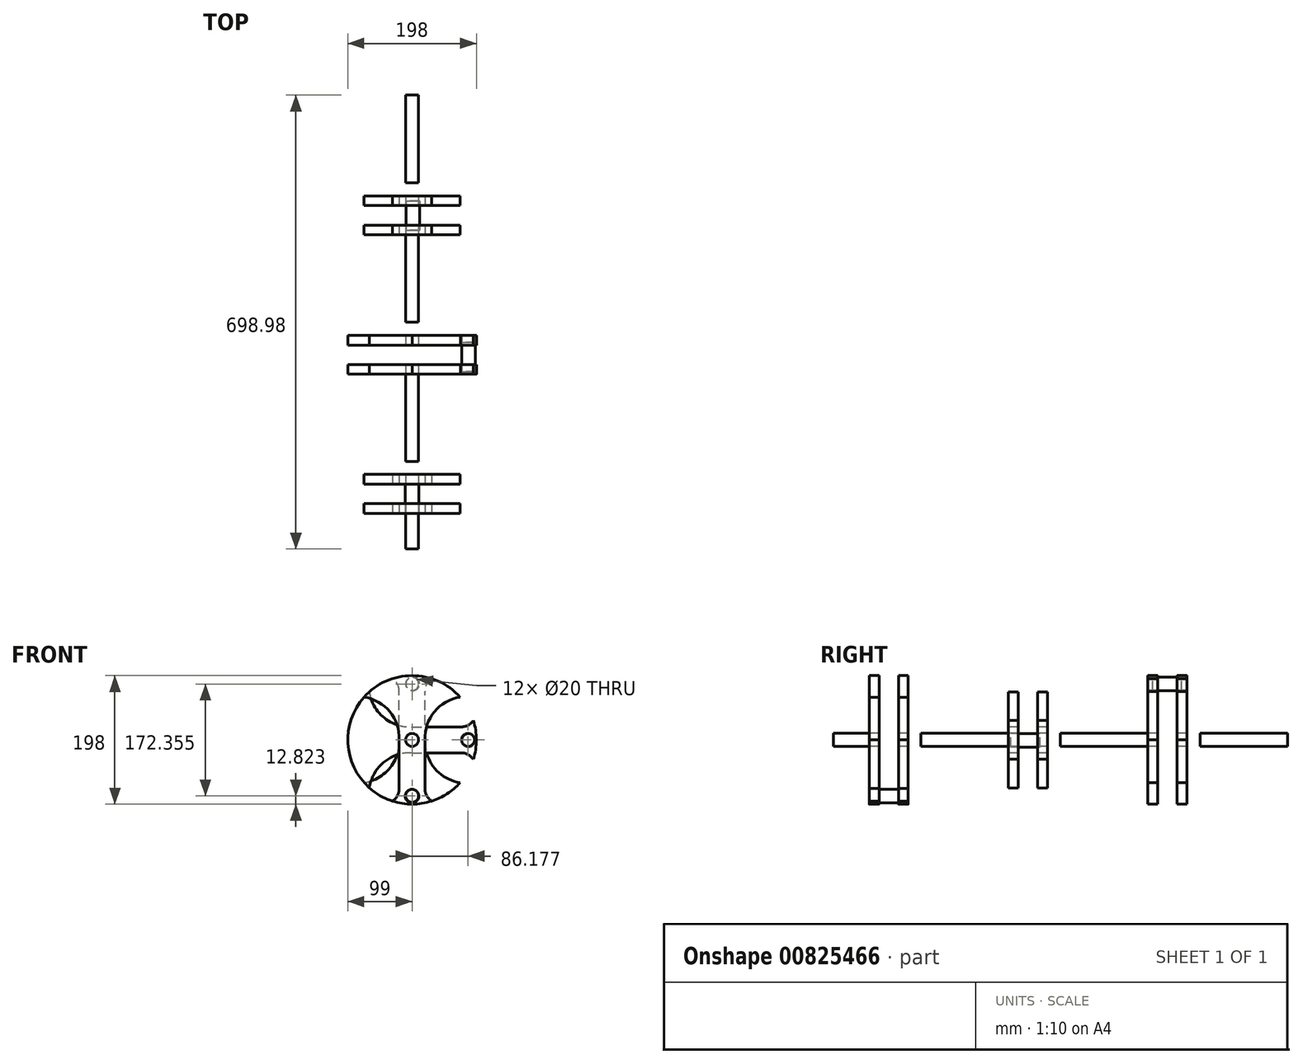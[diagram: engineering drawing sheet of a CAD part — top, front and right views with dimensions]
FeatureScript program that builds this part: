
annotation { "Feature Type Name" : "Feature", "Feature Type Description" : "" }
export const myFeature = defineFeature(function(context is Context, id is Id, definition is map)
    precondition{}
    {
        {
            var Q0;
            Q0=qCreatedBy(makeId("Front.planeOp"),FACE);
            var sketch = newSketch(context, id + "F0", { "sketchPlane" : qUnion([Q0])});
            skCircle(sketch, "E0", {"center": v(0, 0) * mm, "radius": 10 * mm});
            skSolve(sketch);
        }
        {
            var Q0;
            Q0 = qSketchRegion(id + "F0", true);
            extrude(context, id + "F1", {"entities" : qUnion([Q0]), "depth" : 135 * mm, "offsetDistance" : 25 * mm});
        }
        {
            var Q0;
            Q0=makeQuery(id+"F1.opExtrude","CAP_FACE",FACE,{"disambiguationData":[OSD([sQuery(id+"F0.wireOp",EDGE,"E0")])],"isStart":true});
            var sketch = newSketch(context, id + "F2", { "sketchPlane" : qUnion([Q0])});
            skArc(sketch, "E1", {"start": v(-30, -94.35) * mm, "mid": v(0, -99) * mm, "end": v(30, -94.35) * mm});
            skArc(sketch, "E2", {"start": v(-20, 0) * mm, "mid": v(-34.3, 43.3) * mm, "end": v(-73.91, 65.86) * mm});
            skLineSegment(sketch, "E3", {"start": v(-20, 0) * mm, "end": v(-20, -76.74) * mm});
            skArc(sketch, "E4", {"start": v(-30, -94.35) * mm, "mid": v(-22.41, -85.87) * mm, "end": v(-20, -74.76) * mm});
            skArc(sketch, "E5.MirrorCS", {"start": v(20, 0) * mm, "mid": v(34.3, 43.3) * mm, "end": v(73.91, 65.86) * mm});
            skLineSegment(sketch, "E6.MirrorCS", {"start": v(20, 0) * mm, "end": v(20, -76.74) * mm});
            skArc(sketch, "E7.MirrorCS", {"start": v(30, -94.35) * mm, "mid": v(22.41, -85.87) * mm, "end": v(20, -74.76) * mm});
            skArc(sketch, "E8.trimOffspring", {"start": v(73.91, 65.86) * mm, "mid": v(0, 99) * mm, "end": v(-73.91, 65.86) * mm});
            skPoint(sketch, "E9", {"position": v(0, -86.18) * mm});
            skPoint(sketch, "E9.positionSnap0", {"position": v(0, -99) * mm});
            skCircle(sketch, "E10", {"center": v(0, -86.18) * mm, "radius": 10 * mm});
            skSolve(sketch);
        }
        {
            var Q0;
            {var subQ4=sQuery(id+"F2.wireOp",EDGE,"E1");Q0=makeQuery(id+"F2.imprint","IMPRINT",FACE,{"disambiguationData":[TD([[makeQuery(id+"F2.imprint","IMPRINT",EDGE,{"derivedFrom":subQ4}),1.0]])]});}
            extrude(context, id + "F3", {"entities" : qUnion([Q0]), "depth" : 15 * mm, "offsetDistance" : 25 * mm});
        }
        {
            var Q0;
            Q0=makeQuery(id+"F3.opExtrude","SWEPT_BODY",BODY,{"disambiguationData":[OSD([sQuery(id+"F0.wireOp",EDGE,"E0"),sQuery(id+"F2.wireOp",EDGE,"E1"),sQuery(id+"F2.wireOp",EDGE,"E2"),sQuery(id+"F2.wireOp",EDGE,"E3"),sQuery(id+"F2.wireOp",EDGE,"E4"),sQuery(id+"F2.wireOp",EDGE,"E5.MirrorCS"),sQuery(id+"F2.wireOp",EDGE,"E6.MirrorCS"),sQuery(id+"F2.wireOp",EDGE,"E7.MirrorCS"),sQuery(id+"F2.wireOp",EDGE,"E8.trimOffspring"),sQuery(id+"F2.wireOp",EDGE,"E10")])]});
            transform(context, id + "F4", {"entities" : qUnion([Q0]), "transformType" : TransformType.TRANSLATION_3D, "dx" : 0 * mm, "dy" : 0 * mm, "dz" : 0 * mm, "makeCopy" : true});
        }
        {
            var Q0;
            Q0=makeQuery(id+"F3.opExtrude","SWEPT_BODY",BODY,{"disambiguationData":[OSD([sQuery(id+"F0.wireOp",EDGE,"E0"),sQuery(id+"F2.wireOp",EDGE,"E1"),sQuery(id+"F2.wireOp",EDGE,"E2"),sQuery(id+"F2.wireOp",EDGE,"E3"),sQuery(id+"F2.wireOp",EDGE,"E4"),sQuery(id+"F2.wireOp",EDGE,"E5.MirrorCS"),sQuery(id+"F2.wireOp",EDGE,"E6.MirrorCS"),sQuery(id+"F2.wireOp",EDGE,"E7.MirrorCS"),sQuery(id+"F2.wireOp",EDGE,"E8.trimOffspring"),sQuery(id+"F2.wireOp",EDGE,"E10")])]});
            transform(context, id + "F5", {"entities" : qUnion([Q0]), "transformType" : TransformType.TRANSLATION_3D, "dx" : 0 * mm, "dy" : 0 * mm, "dz" : 36 * mm, "makeCopy" : true});
        }
        {
            var Q0;
            Q0=makeQuery(id+"F5.opPattern","COPY",BODY,{"derivedFrom":makeQuery(id+"F3.opExtrude","SWEPT_BODY",BODY,{"disambiguationData":[OSD([sQuery(id+"F0.wireOp",EDGE,"E0"),sQuery(id+"F2.wireOp",EDGE,"E1"),sQuery(id+"F2.wireOp",EDGE,"E2"),sQuery(id+"F2.wireOp",EDGE,"E3"),sQuery(id+"F2.wireOp",EDGE,"E4"),sQuery(id+"F2.wireOp",EDGE,"E5.MirrorCS"),sQuery(id+"F2.wireOp",EDGE,"E6.MirrorCS"),sQuery(id+"F2.wireOp",EDGE,"E7.MirrorCS"),sQuery(id+"F2.wireOp",EDGE,"E8.trimOffspring"),sQuery(id+"F2.wireOp",EDGE,"E10")])]}),"instanceName":"1"});
            deleteBodies(context, id + "F6", {"entities" : qUnion([Q0])});
        }
        {
            var Q0;
            Q0=makeQuery(id+"F4.opPattern","COPY",BODY,{"derivedFrom":makeQuery(id+"F3.opExtrude","SWEPT_BODY",BODY,{"disambiguationData":[OSD([sQuery(id+"F0.wireOp",EDGE,"E0"),sQuery(id+"F2.wireOp",EDGE,"E1"),sQuery(id+"F2.wireOp",EDGE,"E2"),sQuery(id+"F2.wireOp",EDGE,"E3"),sQuery(id+"F2.wireOp",EDGE,"E4"),sQuery(id+"F2.wireOp",EDGE,"E5.MirrorCS"),sQuery(id+"F2.wireOp",EDGE,"E6.MirrorCS"),sQuery(id+"F2.wireOp",EDGE,"E7.MirrorCS"),sQuery(id+"F2.wireOp",EDGE,"E8.trimOffspring"),sQuery(id+"F2.wireOp",EDGE,"E10")])]}),"instanceName":"1"});
            deleteBodies(context, id + "F7", {"entities" : qUnion([Q0])});
        }
        {
            var Q0;
            Q0=makeQuery(id+"F3.opExtrude","SWEPT_BODY",BODY,{"disambiguationData":[OSD([sQuery(id+"F0.wireOp",EDGE,"E0"),sQuery(id+"F2.wireOp",EDGE,"E1"),sQuery(id+"F2.wireOp",EDGE,"E2"),sQuery(id+"F2.wireOp",EDGE,"E3"),sQuery(id+"F2.wireOp",EDGE,"E4"),sQuery(id+"F2.wireOp",EDGE,"E5.MirrorCS"),sQuery(id+"F2.wireOp",EDGE,"E6.MirrorCS"),sQuery(id+"F2.wireOp",EDGE,"E7.MirrorCS"),sQuery(id+"F2.wireOp",EDGE,"E8.trimOffspring"),sQuery(id+"F2.wireOp",EDGE,"E10")])]});
            transform(context, id + "F8", {"entities" : qUnion([Q0]), "transformType" : TransformType.TRANSLATION_3D, "dx" : 36 * mm, "dy" : 0 * mm, "dz" : 0 * mm, "makeCopy" : true});
        }
        {
            var Q0;
            Q0=makeQuery(id+"F8.opPattern","COPY",BODY,{"derivedFrom":makeQuery(id+"F3.opExtrude","SWEPT_BODY",BODY,{"disambiguationData":[OSD([sQuery(id+"F0.wireOp",EDGE,"E0"),sQuery(id+"F2.wireOp",EDGE,"E1"),sQuery(id+"F2.wireOp",EDGE,"E2"),sQuery(id+"F2.wireOp",EDGE,"E3"),sQuery(id+"F2.wireOp",EDGE,"E4"),sQuery(id+"F2.wireOp",EDGE,"E5.MirrorCS"),sQuery(id+"F2.wireOp",EDGE,"E6.MirrorCS"),sQuery(id+"F2.wireOp",EDGE,"E7.MirrorCS"),sQuery(id+"F2.wireOp",EDGE,"E8.trimOffspring"),sQuery(id+"F2.wireOp",EDGE,"E10")])]}),"instanceName":"1"});
            deleteBodies(context, id + "F9", {"entities" : qUnion([Q0])});
        }
        {
            var Q0;
            Q0=makeQuery(id+"F3.opExtrude","SWEPT_BODY",BODY,{"disambiguationData":[OSD([sQuery(id+"F0.wireOp",EDGE,"E0"),sQuery(id+"F2.wireOp",EDGE,"E1"),sQuery(id+"F2.wireOp",EDGE,"E2"),sQuery(id+"F2.wireOp",EDGE,"E3"),sQuery(id+"F2.wireOp",EDGE,"E4"),sQuery(id+"F2.wireOp",EDGE,"E5.MirrorCS"),sQuery(id+"F2.wireOp",EDGE,"E6.MirrorCS"),sQuery(id+"F2.wireOp",EDGE,"E7.MirrorCS"),sQuery(id+"F2.wireOp",EDGE,"E8.trimOffspring"),sQuery(id+"F2.wireOp",EDGE,"E10")])]});
            transform(context, id + "F10", {"entities" : qUnion([Q0]), "transformType" : TransformType.TRANSLATION_3D, "dx" : 0 * mm, "dy" : 36 * mm, "dz" : 0 * mm, "makeCopy" : true});
        }
        {
            var Q0;
            Q0=makeQuery(id+"F10.opPattern","COPY",BODY,{"derivedFrom":makeQuery(id+"F3.opExtrude","SWEPT_BODY",BODY,{"disambiguationData":[OSD([sQuery(id+"F0.wireOp",EDGE,"E0"),sQuery(id+"F2.wireOp",EDGE,"E1"),sQuery(id+"F2.wireOp",EDGE,"E2"),sQuery(id+"F2.wireOp",EDGE,"E3"),sQuery(id+"F2.wireOp",EDGE,"E4"),sQuery(id+"F2.wireOp",EDGE,"E5.MirrorCS"),sQuery(id+"F2.wireOp",EDGE,"E6.MirrorCS"),sQuery(id+"F2.wireOp",EDGE,"E7.MirrorCS"),sQuery(id+"F2.wireOp",EDGE,"E8.trimOffspring"),sQuery(id+"F2.wireOp",EDGE,"E10")])]}),"instanceName":"1"});
            deleteBodies(context, id + "F11", {"entities" : qUnion([Q0])});
        }
        {
            var Q0;
            Q0=qCreatedBy(makeId("Front.planeOp"),FACE);
            var sketch = newSketch(context, id + "F12", { "sketchPlane" : qUnion([Q0])});
            skCircle(sketch, "E11", {"center": v(0, -86.64) * mm, "radius": 10.47 * mm});
            skSolve(sketch);
        }
        {
            var Q0;
            Q0=makeQuery(id+"F12.imprint","IMPRINT",FACE,{"disambiguationData":[TD([[makeQuery(id+"F12.imprint","IMPRINT",EDGE,{"derivedFrom":sQuery(id+"F12.wireOp",EDGE,"E11")}),1.0]])]});
            var Q1;
            Q1=sQuery(id+"F12.wireOp",EDGE,"E11");
            extrude(context, id + "F13", {"entities" : qUnion([Q0]), "surfaceEntities" : qUnion([Q1]), "oppositeDirection" : true, "depth" : 45 * mm, "offsetDistance" : 25 * mm});
        }
        {
            var Q0;
            Q0=makeQuery(id+"F3.opExtrude","SWEPT_BODY",BODY,{"disambiguationData":[OSD([sQuery(id+"F0.wireOp",EDGE,"E0"),sQuery(id+"F2.wireOp",EDGE,"E1"),sQuery(id+"F2.wireOp",EDGE,"E2"),sQuery(id+"F2.wireOp",EDGE,"E3"),sQuery(id+"F2.wireOp",EDGE,"E4"),sQuery(id+"F2.wireOp",EDGE,"E5.MirrorCS"),sQuery(id+"F2.wireOp",EDGE,"E6.MirrorCS"),sQuery(id+"F2.wireOp",EDGE,"E7.MirrorCS"),sQuery(id+"F2.wireOp",EDGE,"E8.trimOffspring"),sQuery(id+"F2.wireOp",EDGE,"E10")])]});
            transform(context, id + "F14", {"entities" : qUnion([Q0]), "transformType" : TransformType.TRANSLATION_3D, "dx" : 0 * mm, "dy" : 30.5 * mm, "dz" : 0 * mm, "makeCopy" : true});
        }
        {
            var Q0;
            Q0=makeQuery(id+"F1.opExtrude","SWEPT_BODY",BODY,{"disambiguationData":[OSD([sQuery(id+"F0.wireOp",EDGE,"E0")])]});
            transform(context, id + "F15", {"entities" : qUnion([Q0]), "transformType" : TransformType.TRANSLATION_3D, "dx" : 0 * mm, "dy" : 131.5 * mm, "dz" : 0 * mm, "makeCopy" : true});
        }
        {
            var Q0;
            Q0=makeQuery(id+"F15.opPattern","COPY",BODY,{"derivedFrom":makeQuery(id+"F1.opExtrude","SWEPT_BODY",BODY,{"disambiguationData":[OSD([sQuery(id+"F0.wireOp",EDGE,"E0")])]}),"instanceName":"1"});
            deleteBodies(context, id + "F16", {"entities" : qUnion([Q0])});
        }
        {
            var Q0;
            Q0=makeQuery(id+"F3.opExtrude","SWEPT_BODY",BODY,{"disambiguationData":[OSD([sQuery(id+"F0.wireOp",EDGE,"E0"),sQuery(id+"F2.wireOp",EDGE,"E1"),sQuery(id+"F2.wireOp",EDGE,"E2"),sQuery(id+"F2.wireOp",EDGE,"E3"),sQuery(id+"F2.wireOp",EDGE,"E4"),sQuery(id+"F2.wireOp",EDGE,"E5.MirrorCS"),sQuery(id+"F2.wireOp",EDGE,"E6.MirrorCS"),sQuery(id+"F2.wireOp",EDGE,"E7.MirrorCS"),sQuery(id+"F2.wireOp",EDGE,"E8.trimOffspring"),sQuery(id+"F2.wireOp",EDGE,"E10")])]});
            transform(context, id + "F17", {"entities" : qUnion([Q0]), "transformType" : TransformType.TRANSLATION_3D, "dx" : 0 * mm, "dy" : 46 * mm, "dz" : 0 * mm, "makeCopy" : true});
        }
        {
            var Q0;
            Q0=makeQuery(id+"F17.opPattern","COPY",BODY,{"derivedFrom":makeQuery(id+"F3.opExtrude","SWEPT_BODY",BODY,{"disambiguationData":[OSD([sQuery(id+"F0.wireOp",EDGE,"E0"),sQuery(id+"F2.wireOp",EDGE,"E1"),sQuery(id+"F2.wireOp",EDGE,"E2"),sQuery(id+"F2.wireOp",EDGE,"E3"),sQuery(id+"F2.wireOp",EDGE,"E4"),sQuery(id+"F2.wireOp",EDGE,"E5.MirrorCS"),sQuery(id+"F2.wireOp",EDGE,"E6.MirrorCS"),sQuery(id+"F2.wireOp",EDGE,"E7.MirrorCS"),sQuery(id+"F2.wireOp",EDGE,"E8.trimOffspring"),sQuery(id+"F2.wireOp",EDGE,"E10")])]}),"instanceName":"1"});
            var Q1;
            Q1=makeQuery(id+"F17.opPattern","COPY",EDGE,{"derivedFrom":makeQuery(id+"F3.opExtrude","CAP_EDGE",EDGE,{"disambiguationData":[OSD([sQuery(id+"F0.wireOp",EDGE,"E0")])],"isStart":false}),"instanceName":"1"});
            transform(context, id + "F18", {"entities" : qUnion([Q0]), "transformType" : TransformType.ROTATION, "transformAxis" : qUnion([Q1]), "angle" : 45 * degree, "makeCopy" : false});
        }
        {
            var Q0;
            Q0=makeQuery(id+"F13.opExtrude","SWEPT_BODY",BODY,{"disambiguationData":[OSD([sQuery(id+"F12.wireOp",EDGE,"E11")])]});
            transform(context, id + "F19", {"entities" : qUnion([Q0]), "transformType" : TransformType.TRANSLATION_3D, "dx" : 61 * mm, "dy" : 46 * mm, "dz" : 26 * mm, "makeCopy" : true});
        }
        {
            var Q0;
            Q0=makeQuery(id+"F17.opPattern","COPY",BODY,{"derivedFrom":makeQuery(id+"F3.opExtrude","SWEPT_BODY",BODY,{"disambiguationData":[OSD([sQuery(id+"F0.wireOp",EDGE,"E0"),sQuery(id+"F2.wireOp",EDGE,"E1"),sQuery(id+"F2.wireOp",EDGE,"E2"),sQuery(id+"F2.wireOp",EDGE,"E3"),sQuery(id+"F2.wireOp",EDGE,"E4"),sQuery(id+"F2.wireOp",EDGE,"E5.MirrorCS"),sQuery(id+"F2.wireOp",EDGE,"E6.MirrorCS"),sQuery(id+"F2.wireOp",EDGE,"E7.MirrorCS"),sQuery(id+"F2.wireOp",EDGE,"E8.trimOffspring"),sQuery(id+"F2.wireOp",EDGE,"E10")])]}),"instanceName":"1"});
            transform(context, id + "F20", {"entities" : qUnion([Q0]), "transformType" : TransformType.TRANSLATION_3D, "dx" : 0 * mm, "dy" : 31.5 * mm, "dz" : 0 * mm, "makeCopy" : true});
        }
        {
            var Q0;
            Q0=makeQuery(id+"F20.opPattern","COPY",BODY,{"derivedFrom":makeQuery(id+"F17.opPattern","COPY",BODY,{"derivedFrom":makeQuery(id+"F3.opExtrude","SWEPT_BODY",BODY,{"disambiguationData":[OSD([sQuery(id+"F0.wireOp",EDGE,"E0"),sQuery(id+"F2.wireOp",EDGE,"E1"),sQuery(id+"F2.wireOp",EDGE,"E2"),sQuery(id+"F2.wireOp",EDGE,"E3"),sQuery(id+"F2.wireOp",EDGE,"E4"),sQuery(id+"F2.wireOp",EDGE,"E5.MirrorCS"),sQuery(id+"F2.wireOp",EDGE,"E6.MirrorCS"),sQuery(id+"F2.wireOp",EDGE,"E7.MirrorCS"),sQuery(id+"F2.wireOp",EDGE,"E8.trimOffspring"),sQuery(id+"F2.wireOp",EDGE,"E10")])]}),"instanceName":"1"}),"instanceName":"1"});
            transform(context, id + "F21", {"entities" : qUnion([Q0]), "transformType" : TransformType.TRANSLATION_3D, "dx" : 0 * mm, "dy" : 136.66 * mm, "dz" : 0 * mm, "makeCopy" : true});
        }
        {
            var Q0;
            Q0=makeQuery(id+"F21.opPattern","COPY",BODY,{"derivedFrom":makeQuery(id+"F20.opPattern","COPY",BODY,{"derivedFrom":makeQuery(id+"F17.opPattern","COPY",BODY,{"derivedFrom":makeQuery(id+"F3.opExtrude","SWEPT_BODY",BODY,{"disambiguationData":[OSD([sQuery(id+"F0.wireOp",EDGE,"E0"),sQuery(id+"F2.wireOp",EDGE,"E1"),sQuery(id+"F2.wireOp",EDGE,"E2"),sQuery(id+"F2.wireOp",EDGE,"E3"),sQuery(id+"F2.wireOp",EDGE,"E4"),sQuery(id+"F2.wireOp",EDGE,"E5.MirrorCS"),sQuery(id+"F2.wireOp",EDGE,"E6.MirrorCS"),sQuery(id+"F2.wireOp",EDGE,"E7.MirrorCS"),sQuery(id+"F2.wireOp",EDGE,"E8.trimOffspring"),sQuery(id+"F2.wireOp",EDGE,"E10")])]}),"instanceName":"1"}),"instanceName":"1"}),"instanceName":"1"});
            var Q1;
            Q1=makeQuery(id+"F21.opPattern","COPY",EDGE,{"derivedFrom":makeQuery(id+"F20.opPattern","COPY",EDGE,{"derivedFrom":makeQuery(id+"F17.opPattern","COPY",EDGE,{"derivedFrom":makeQuery(id+"F3.opExtrude","CAP_EDGE",EDGE,{"disambiguationData":[OSD([sQuery(id+"F0.wireOp",EDGE,"E0")])],"isStart":false}),"instanceName":"1"}),"instanceName":"1"}),"instanceName":"1"});
            transform(context, id + "F22", {"entities" : qUnion([Q0]), "transformType" : TransformType.ROTATION, "transformAxis" : qUnion([Q1]), "angle" : 45 * degree, "makeCopy" : false});
        }
        {
            var Q0;
            Q0=makeQuery(id+"F1.opExtrude","SWEPT_BODY",BODY,{"disambiguationData":[OSD([sQuery(id+"F0.wireOp",EDGE,"E0")])]});
            transform(context, id + "F23", {"entities" : qUnion([Q0]), "transformType" : TransformType.TRANSLATION_3D, "dx" : 0 * mm, "dy" : 214.66 * mm, "dz" : 0 * mm, "makeCopy" : true});
        }
        {
            var Q0;
            Q0=makeQuery(id+"F21.opPattern","COPY",BODY,{"derivedFrom":makeQuery(id+"F20.opPattern","COPY",BODY,{"derivedFrom":makeQuery(id+"F17.opPattern","COPY",BODY,{"derivedFrom":makeQuery(id+"F3.opExtrude","SWEPT_BODY",BODY,{"disambiguationData":[OSD([sQuery(id+"F0.wireOp",EDGE,"E0"),sQuery(id+"F2.wireOp",EDGE,"E1"),sQuery(id+"F2.wireOp",EDGE,"E2"),sQuery(id+"F2.wireOp",EDGE,"E3"),sQuery(id+"F2.wireOp",EDGE,"E4"),sQuery(id+"F2.wireOp",EDGE,"E5.MirrorCS"),sQuery(id+"F2.wireOp",EDGE,"E6.MirrorCS"),sQuery(id+"F2.wireOp",EDGE,"E7.MirrorCS"),sQuery(id+"F2.wireOp",EDGE,"E8.trimOffspring"),sQuery(id+"F2.wireOp",EDGE,"E10")])]}),"instanceName":"1"}),"instanceName":"1"}),"instanceName":"1"});
            transform(context, id + "F24", {"entities" : qUnion([Q0]), "transformType" : TransformType.TRANSLATION_3D, "dx" : 0 * mm, "dy" : 31.5 * mm, "dz" : 0 * mm, "makeCopy" : true});
        }
        {
            var Q0;
            Q0=makeQuery(id+"F19.opPattern","COPY",BODY,{"derivedFrom":makeQuery(id+"F13.opExtrude","SWEPT_BODY",BODY,{"disambiguationData":[OSD([sQuery(id+"F12.wireOp",EDGE,"E11")])]}),"instanceName":"1"});
            transform(context, id + "F25", {"entities" : qUnion([Q0]), "transformType" : TransformType.TRANSLATION_3D, "dx" : 26 * mm, "dy" : 172 * mm, "dz" : 60 * mm, "makeCopy" : true});
        }
        {
            var Q0;
            Q0=makeQuery(id+"F24.opPattern","COPY",BODY,{"derivedFrom":makeQuery(id+"F21.opPattern","COPY",BODY,{"derivedFrom":makeQuery(id+"F20.opPattern","COPY",BODY,{"derivedFrom":makeQuery(id+"F17.opPattern","COPY",BODY,{"derivedFrom":makeQuery(id+"F3.opExtrude","SWEPT_BODY",BODY,{"disambiguationData":[OSD([sQuery(id+"F0.wireOp",EDGE,"E0"),sQuery(id+"F2.wireOp",EDGE,"E1"),sQuery(id+"F2.wireOp",EDGE,"E2"),sQuery(id+"F2.wireOp",EDGE,"E3"),sQuery(id+"F2.wireOp",EDGE,"E4"),sQuery(id+"F2.wireOp",EDGE,"E5.MirrorCS"),sQuery(id+"F2.wireOp",EDGE,"E6.MirrorCS"),sQuery(id+"F2.wireOp",EDGE,"E7.MirrorCS"),sQuery(id+"F2.wireOp",EDGE,"E8.trimOffspring"),sQuery(id+"F2.wireOp",EDGE,"E10")])]}),"instanceName":"1"}),"instanceName":"1"}),"instanceName":"1"}),"instanceName":"1"});
            transform(context, id + "F26", {"entities" : qUnion([Q0]), "transformType" : TransformType.TRANSLATION_3D, "dx" : 0 * mm, "dy" : 15 * mm, "dz" : 0 * mm, "makeCopy" : true});
        }
        {
            var Q0;
            Q0=makeQuery(id+"F26.opPattern","COPY",BODY,{"derivedFrom":makeQuery(id+"F24.opPattern","COPY",BODY,{"derivedFrom":makeQuery(id+"F21.opPattern","COPY",BODY,{"derivedFrom":makeQuery(id+"F20.opPattern","COPY",BODY,{"derivedFrom":makeQuery(id+"F17.opPattern","COPY",BODY,{"derivedFrom":makeQuery(id+"F3.opExtrude","SWEPT_BODY",BODY,{"disambiguationData":[OSD([sQuery(id+"F0.wireOp",EDGE,"E0"),sQuery(id+"F2.wireOp",EDGE,"E1"),sQuery(id+"F2.wireOp",EDGE,"E2"),sQuery(id+"F2.wireOp",EDGE,"E3"),sQuery(id+"F2.wireOp",EDGE,"E4"),sQuery(id+"F2.wireOp",EDGE,"E5.MirrorCS"),sQuery(id+"F2.wireOp",EDGE,"E6.MirrorCS"),sQuery(id+"F2.wireOp",EDGE,"E7.MirrorCS"),sQuery(id+"F2.wireOp",EDGE,"E8.trimOffspring"),sQuery(id+"F2.wireOp",EDGE,"E10")])]}),"instanceName":"1"}),"instanceName":"1"}),"instanceName":"1"}),"instanceName":"1"}),"instanceName":"1"});
            var Q1;
            Q1=makeQuery(id+"F26.opPattern","COPY",EDGE,{"derivedFrom":makeQuery(id+"F24.opPattern","COPY",EDGE,{"derivedFrom":makeQuery(id+"F21.opPattern","COPY",EDGE,{"derivedFrom":makeQuery(id+"F20.opPattern","COPY",EDGE,{"derivedFrom":makeQuery(id+"F17.opPattern","COPY",EDGE,{"derivedFrom":makeQuery(id+"F3.opExtrude","CAP_EDGE",EDGE,{"disambiguationData":[OSD([sQuery(id+"F0.wireOp",EDGE,"E0")])],"isStart":false}),"instanceName":"1"}),"instanceName":"1"}),"instanceName":"1"}),"instanceName":"1"}),"instanceName":"1"});
            transform(context, id + "F27", {"entities" : qUnion([Q0]), "transformType" : TransformType.ROTATION, "transformAxis" : qUnion([Q1]), "angle" : 45 * degree, "makeCopy" : false});
        }
        {
            var Q0;
            Q0=makeQuery(id+"F26.opPattern","COPY",BODY,{"derivedFrom":makeQuery(id+"F24.opPattern","COPY",BODY,{"derivedFrom":makeQuery(id+"F21.opPattern","COPY",BODY,{"derivedFrom":makeQuery(id+"F20.opPattern","COPY",BODY,{"derivedFrom":makeQuery(id+"F17.opPattern","COPY",BODY,{"derivedFrom":makeQuery(id+"F3.opExtrude","SWEPT_BODY",BODY,{"disambiguationData":[OSD([sQuery(id+"F0.wireOp",EDGE,"E0"),sQuery(id+"F2.wireOp",EDGE,"E1"),sQuery(id+"F2.wireOp",EDGE,"E2"),sQuery(id+"F2.wireOp",EDGE,"E3"),sQuery(id+"F2.wireOp",EDGE,"E4"),sQuery(id+"F2.wireOp",EDGE,"E5.MirrorCS"),sQuery(id+"F2.wireOp",EDGE,"E6.MirrorCS"),sQuery(id+"F2.wireOp",EDGE,"E7.MirrorCS"),sQuery(id+"F2.wireOp",EDGE,"E8.trimOffspring"),sQuery(id+"F2.wireOp",EDGE,"E10")])]}),"instanceName":"1"}),"instanceName":"1"}),"instanceName":"1"}),"instanceName":"1"}),"instanceName":"1"});
            transform(context, id + "F28", {"entities" : qUnion([Q0]), "transformType" : TransformType.TRANSLATION_3D, "dx" : 0 * mm, "dy" : 31.5 * mm, "dz" : 0 * mm, "makeCopy" : true});
        }
        {
            var Q0;
            Q0=makeQuery(id+"F25.opPattern","COPY",BODY,{"derivedFrom":makeQuery(id+"F19.opPattern","COPY",BODY,{"derivedFrom":makeQuery(id+"F13.opExtrude","SWEPT_BODY",BODY,{"disambiguationData":[OSD([sQuery(id+"F12.wireOp",EDGE,"E11")])]}),"instanceName":"1"}),"instanceName":"1"});
            transform(context, id + "F29", {"entities" : qUnion([Q0]), "transformType" : TransformType.TRANSLATION_3D, "dx" : -26 * mm, "dy" : 47 * mm, "dz" : 61 * mm, "makeCopy" : true});
        }
        {
            var Q0;
            Q0=makeQuery(id+"F23.opPattern","COPY",BODY,{"derivedFrom":makeQuery(id+"F1.opExtrude","SWEPT_BODY",BODY,{"disambiguationData":[OSD([sQuery(id+"F0.wireOp",EDGE,"E0")])]}),"instanceName":"1"});
            transform(context, id + "F30", {"entities" : qUnion([Q0]), "transformType" : TransformType.TRANSLATION_3D, "dx" : 0 * mm, "dy" : 214.66 * mm, "dz" : 0 * mm, "makeCopy" : true});
        }
        {
            var Q0;
            Q0=makeQuery(id+"F28.opPattern","COPY",BODY,{"derivedFrom":makeQuery(id+"F26.opPattern","COPY",BODY,{"derivedFrom":makeQuery(id+"F24.opPattern","COPY",BODY,{"derivedFrom":makeQuery(id+"F21.opPattern","COPY",BODY,{"derivedFrom":makeQuery(id+"F20.opPattern","COPY",BODY,{"derivedFrom":makeQuery(id+"F17.opPattern","COPY",BODY,{"derivedFrom":makeQuery(id+"F3.opExtrude","SWEPT_BODY",BODY,{"disambiguationData":[OSD([sQuery(id+"F0.wireOp",EDGE,"E0"),sQuery(id+"F2.wireOp",EDGE,"E1"),sQuery(id+"F2.wireOp",EDGE,"E2"),sQuery(id+"F2.wireOp",EDGE,"E3"),sQuery(id+"F2.wireOp",EDGE,"E4"),sQuery(id+"F2.wireOp",EDGE,"E5.MirrorCS"),sQuery(id+"F2.wireOp",EDGE,"E6.MirrorCS"),sQuery(id+"F2.wireOp",EDGE,"E7.MirrorCS"),sQuery(id+"F2.wireOp",EDGE,"E8.trimOffspring"),sQuery(id+"F2.wireOp",EDGE,"E10")])]}),"instanceName":"1"}),"instanceName":"1"}),"instanceName":"1"}),"instanceName":"1"}),"instanceName":"1"}),"instanceName":"1"});
            transform(context, id + "F31", {"entities" : qUnion([Q0]), "transformType" : TransformType.TRANSLATION_3D, "dx" : 0 * mm, "dy" : 136.66 * mm, "dz" : 0 * mm, "makeCopy" : true});
        }
        {
            var Q0;
            Q0=makeQuery(id+"F31.opPattern","COPY",BODY,{"derivedFrom":makeQuery(id+"F28.opPattern","COPY",BODY,{"derivedFrom":makeQuery(id+"F26.opPattern","COPY",BODY,{"derivedFrom":makeQuery(id+"F24.opPattern","COPY",BODY,{"derivedFrom":makeQuery(id+"F21.opPattern","COPY",BODY,{"derivedFrom":makeQuery(id+"F20.opPattern","COPY",BODY,{"derivedFrom":makeQuery(id+"F17.opPattern","COPY",BODY,{"derivedFrom":makeQuery(id+"F3.opExtrude","SWEPT_BODY",BODY,{"disambiguationData":[OSD([sQuery(id+"F0.wireOp",EDGE,"E0"),sQuery(id+"F2.wireOp",EDGE,"E1"),sQuery(id+"F2.wireOp",EDGE,"E2"),sQuery(id+"F2.wireOp",EDGE,"E3"),sQuery(id+"F2.wireOp",EDGE,"E4"),sQuery(id+"F2.wireOp",EDGE,"E5.MirrorCS"),sQuery(id+"F2.wireOp",EDGE,"E6.MirrorCS"),sQuery(id+"F2.wireOp",EDGE,"E7.MirrorCS"),sQuery(id+"F2.wireOp",EDGE,"E8.trimOffspring"),sQuery(id+"F2.wireOp",EDGE,"E10")])]}),"instanceName":"1"}),"instanceName":"1"}),"instanceName":"1"}),"instanceName":"1"}),"instanceName":"1"}),"instanceName":"1"}),"instanceName":"1"});
            var Q1;
            Q1=makeQuery(id+"F31.opPattern","COPY",EDGE,{"derivedFrom":makeQuery(id+"F28.opPattern","COPY",EDGE,{"derivedFrom":makeQuery(id+"F26.opPattern","COPY",EDGE,{"derivedFrom":makeQuery(id+"F24.opPattern","COPY",EDGE,{"derivedFrom":makeQuery(id+"F21.opPattern","COPY",EDGE,{"derivedFrom":makeQuery(id+"F20.opPattern","COPY",EDGE,{"derivedFrom":makeQuery(id+"F17.opPattern","COPY",EDGE,{"derivedFrom":makeQuery(id+"F3.opExtrude","CAP_EDGE",EDGE,{"disambiguationData":[OSD([sQuery(id+"F0.wireOp",EDGE,"E0")])],"isStart":false}),"instanceName":"1"}),"instanceName":"1"}),"instanceName":"1"}),"instanceName":"1"}),"instanceName":"1"}),"instanceName":"1"}),"instanceName":"1"});
            transform(context, id + "F32", {"entities" : qUnion([Q0]), "transformType" : TransformType.ROTATION, "transformAxis" : qUnion([Q1]), "angle" : 45 * degree, "makeCopy" : false});
        }
        {
            var Q0;
            Q0=makeQuery(id+"F31.opPattern","COPY",BODY,{"derivedFrom":makeQuery(id+"F28.opPattern","COPY",BODY,{"derivedFrom":makeQuery(id+"F26.opPattern","COPY",BODY,{"derivedFrom":makeQuery(id+"F24.opPattern","COPY",BODY,{"derivedFrom":makeQuery(id+"F21.opPattern","COPY",BODY,{"derivedFrom":makeQuery(id+"F20.opPattern","COPY",BODY,{"derivedFrom":makeQuery(id+"F17.opPattern","COPY",BODY,{"derivedFrom":makeQuery(id+"F3.opExtrude","SWEPT_BODY",BODY,{"disambiguationData":[OSD([sQuery(id+"F0.wireOp",EDGE,"E0"),sQuery(id+"F2.wireOp",EDGE,"E1"),sQuery(id+"F2.wireOp",EDGE,"E2"),sQuery(id+"F2.wireOp",EDGE,"E3"),sQuery(id+"F2.wireOp",EDGE,"E4"),sQuery(id+"F2.wireOp",EDGE,"E5.MirrorCS"),sQuery(id+"F2.wireOp",EDGE,"E6.MirrorCS"),sQuery(id+"F2.wireOp",EDGE,"E7.MirrorCS"),sQuery(id+"F2.wireOp",EDGE,"E8.trimOffspring"),sQuery(id+"F2.wireOp",EDGE,"E10")])]}),"instanceName":"1"}),"instanceName":"1"}),"instanceName":"1"}),"instanceName":"1"}),"instanceName":"1"}),"instanceName":"1"}),"instanceName":"1"});
            transform(context, id + "F33", {"entities" : qUnion([Q0]), "transformType" : TransformType.TRANSLATION_3D, "dx" : 0 * mm, "dy" : 31.5 * mm, "dz" : 0 * mm, "makeCopy" : true});
        }
        {
            var Q0;
            Q0=makeQuery(id+"F29.opPattern","COPY",BODY,{"derivedFrom":makeQuery(id+"F25.opPattern","COPY",BODY,{"derivedFrom":makeQuery(id+"F19.opPattern","COPY",BODY,{"derivedFrom":makeQuery(id+"F13.opExtrude","SWEPT_BODY",BODY,{"disambiguationData":[OSD([sQuery(id+"F12.wireOp",EDGE,"E11")])]}),"instanceName":"1"}),"instanceName":"1"}),"instanceName":"1"});
            transform(context, id + "F34", {"entities" : qUnion([Q0]), "transformType" : TransformType.TRANSLATION_3D, "dx" : -60 * mm, "dy" : 171 * mm, "dz" : 26 * mm, "makeCopy" : true});
        }
        {
            var Q0;
            Q0=makeQuery(id+"F33.opPattern","COPY",BODY,{"derivedFrom":makeQuery(id+"F31.opPattern","COPY",BODY,{"derivedFrom":makeQuery(id+"F28.opPattern","COPY",BODY,{"derivedFrom":makeQuery(id+"F26.opPattern","COPY",BODY,{"derivedFrom":makeQuery(id+"F24.opPattern","COPY",BODY,{"derivedFrom":makeQuery(id+"F21.opPattern","COPY",BODY,{"derivedFrom":makeQuery(id+"F20.opPattern","COPY",BODY,{"derivedFrom":makeQuery(id+"F17.opPattern","COPY",BODY,{"derivedFrom":makeQuery(id+"F3.opExtrude","SWEPT_BODY",BODY,{"disambiguationData":[OSD([sQuery(id+"F0.wireOp",EDGE,"E0"),sQuery(id+"F2.wireOp",EDGE,"E1"),sQuery(id+"F2.wireOp",EDGE,"E2"),sQuery(id+"F2.wireOp",EDGE,"E3"),sQuery(id+"F2.wireOp",EDGE,"E4"),sQuery(id+"F2.wireOp",EDGE,"E5.MirrorCS"),sQuery(id+"F2.wireOp",EDGE,"E6.MirrorCS"),sQuery(id+"F2.wireOp",EDGE,"E7.MirrorCS"),sQuery(id+"F2.wireOp",EDGE,"E8.trimOffspring"),sQuery(id+"F2.wireOp",EDGE,"E10")])]}),"instanceName":"1"}),"instanceName":"1"}),"instanceName":"1"}),"instanceName":"1"}),"instanceName":"1"}),"instanceName":"1"}),"instanceName":"1"}),"instanceName":"1"});
            transform(context, id + "F35", {"entities" : qUnion([Q0]), "transformType" : TransformType.TRANSLATION_3D, "dx" : 0 * mm, "dy" : 15 * mm, "dz" : 0 * mm, "makeCopy" : true});
        }
        {
            var Q0;
            Q0=makeQuery(id+"F35.opPattern","COPY",BODY,{"derivedFrom":makeQuery(id+"F33.opPattern","COPY",BODY,{"derivedFrom":makeQuery(id+"F31.opPattern","COPY",BODY,{"derivedFrom":makeQuery(id+"F28.opPattern","COPY",BODY,{"derivedFrom":makeQuery(id+"F26.opPattern","COPY",BODY,{"derivedFrom":makeQuery(id+"F24.opPattern","COPY",BODY,{"derivedFrom":makeQuery(id+"F21.opPattern","COPY",BODY,{"derivedFrom":makeQuery(id+"F20.opPattern","COPY",BODY,{"derivedFrom":makeQuery(id+"F17.opPattern","COPY",BODY,{"derivedFrom":makeQuery(id+"F3.opExtrude","SWEPT_BODY",BODY,{"disambiguationData":[OSD([sQuery(id+"F0.wireOp",EDGE,"E0"),sQuery(id+"F2.wireOp",EDGE,"E1"),sQuery(id+"F2.wireOp",EDGE,"E2"),sQuery(id+"F2.wireOp",EDGE,"E3"),sQuery(id+"F2.wireOp",EDGE,"E4"),sQuery(id+"F2.wireOp",EDGE,"E5.MirrorCS"),sQuery(id+"F2.wireOp",EDGE,"E6.MirrorCS"),sQuery(id+"F2.wireOp",EDGE,"E7.MirrorCS"),sQuery(id+"F2.wireOp",EDGE,"E8.trimOffspring"),sQuery(id+"F2.wireOp",EDGE,"E10")])]}),"instanceName":"1"}),"instanceName":"1"}),"instanceName":"1"}),"instanceName":"1"}),"instanceName":"1"}),"instanceName":"1"}),"instanceName":"1"}),"instanceName":"1"}),"instanceName":"1"});
            var Q1;
            Q1=makeQuery(id+"F35.opPattern","COPY",EDGE,{"derivedFrom":makeQuery(id+"F33.opPattern","COPY",EDGE,{"derivedFrom":makeQuery(id+"F31.opPattern","COPY",EDGE,{"derivedFrom":makeQuery(id+"F28.opPattern","COPY",EDGE,{"derivedFrom":makeQuery(id+"F26.opPattern","COPY",EDGE,{"derivedFrom":makeQuery(id+"F24.opPattern","COPY",EDGE,{"derivedFrom":makeQuery(id+"F21.opPattern","COPY",EDGE,{"derivedFrom":makeQuery(id+"F20.opPattern","COPY",EDGE,{"derivedFrom":makeQuery(id+"F17.opPattern","COPY",EDGE,{"derivedFrom":makeQuery(id+"F3.opExtrude","CAP_EDGE",EDGE,{"disambiguationData":[OSD([sQuery(id+"F0.wireOp",EDGE,"E0")])],"isStart":false}),"instanceName":"1"}),"instanceName":"1"}),"instanceName":"1"}),"instanceName":"1"}),"instanceName":"1"}),"instanceName":"1"}),"instanceName":"1"}),"instanceName":"1"}),"instanceName":"1"});
            transform(context, id + "F36", {"entities" : qUnion([Q0]), "transformType" : TransformType.ROTATION, "transformAxis" : qUnion([Q1]), "angle" : 45 * degree, "makeCopy" : false});
        }
        {
            var Q0;
            Q0=makeQuery(id+"F35.opPattern","COPY",BODY,{"derivedFrom":makeQuery(id+"F33.opPattern","COPY",BODY,{"derivedFrom":makeQuery(id+"F31.opPattern","COPY",BODY,{"derivedFrom":makeQuery(id+"F28.opPattern","COPY",BODY,{"derivedFrom":makeQuery(id+"F26.opPattern","COPY",BODY,{"derivedFrom":makeQuery(id+"F24.opPattern","COPY",BODY,{"derivedFrom":makeQuery(id+"F21.opPattern","COPY",BODY,{"derivedFrom":makeQuery(id+"F20.opPattern","COPY",BODY,{"derivedFrom":makeQuery(id+"F17.opPattern","COPY",BODY,{"derivedFrom":makeQuery(id+"F3.opExtrude","SWEPT_BODY",BODY,{"disambiguationData":[OSD([sQuery(id+"F0.wireOp",EDGE,"E0"),sQuery(id+"F2.wireOp",EDGE,"E1"),sQuery(id+"F2.wireOp",EDGE,"E2"),sQuery(id+"F2.wireOp",EDGE,"E3"),sQuery(id+"F2.wireOp",EDGE,"E4"),sQuery(id+"F2.wireOp",EDGE,"E5.MirrorCS"),sQuery(id+"F2.wireOp",EDGE,"E6.MirrorCS"),sQuery(id+"F2.wireOp",EDGE,"E7.MirrorCS"),sQuery(id+"F2.wireOp",EDGE,"E8.trimOffspring"),sQuery(id+"F2.wireOp",EDGE,"E10")])]}),"instanceName":"1"}),"instanceName":"1"}),"instanceName":"1"}),"instanceName":"1"}),"instanceName":"1"}),"instanceName":"1"}),"instanceName":"1"}),"instanceName":"1"}),"instanceName":"1"});
            transform(context, id + "F37", {"entities" : qUnion([Q0]), "transformType" : TransformType.TRANSLATION_3D, "dx" : 0 * mm, "dy" : 31.5 * mm, "dz" : 0 * mm, "makeCopy" : true});
        }
        {
            var Q0;
            Q0=makeQuery(id+"F34.opPattern","COPY",BODY,{"derivedFrom":makeQuery(id+"F29.opPattern","COPY",BODY,{"derivedFrom":makeQuery(id+"F25.opPattern","COPY",BODY,{"derivedFrom":makeQuery(id+"F19.opPattern","COPY",BODY,{"derivedFrom":makeQuery(id+"F13.opExtrude","SWEPT_BODY",BODY,{"disambiguationData":[OSD([sQuery(id+"F12.wireOp",EDGE,"E11")])]}),"instanceName":"1"}),"instanceName":"1"}),"instanceName":"1"}),"instanceName":"1"});
            transform(context, id + "F38", {"entities" : qUnion([Q0]), "transformType" : TransformType.TRANSLATION_3D, "dx" : -61 * mm, "dy" : 43 * mm, "dz" : -25 * mm, "makeCopy" : true});
        }
        {
            var Q0;
            Q0=makeQuery(id+"F30.opPattern","COPY",BODY,{"derivedFrom":makeQuery(id+"F23.opPattern","COPY",BODY,{"derivedFrom":makeQuery(id+"F1.opExtrude","SWEPT_BODY",BODY,{"disambiguationData":[OSD([sQuery(id+"F0.wireOp",EDGE,"E0")])]}),"instanceName":"1"}),"instanceName":"1"});
            transform(context, id + "F39", {"entities" : qUnion([Q0]), "transformType" : TransformType.TRANSLATION_3D, "dx" : 0 * mm, "dy" : 214.66 * mm, "dz" : 0 * mm, "makeCopy" : true});
        }
        {
            var Q0;
            Q0=makeQuery(id+"F14.opPattern","COPY",BODY,{"derivedFrom":makeQuery(id+"F3.opExtrude","SWEPT_BODY",BODY,{"disambiguationData":[OSD([sQuery(id+"F0.wireOp",EDGE,"E0"),sQuery(id+"F2.wireOp",EDGE,"E1"),sQuery(id+"F2.wireOp",EDGE,"E2"),sQuery(id+"F2.wireOp",EDGE,"E3"),sQuery(id+"F2.wireOp",EDGE,"E4"),sQuery(id+"F2.wireOp",EDGE,"E5.MirrorCS"),sQuery(id+"F2.wireOp",EDGE,"E6.MirrorCS"),sQuery(id+"F2.wireOp",EDGE,"E7.MirrorCS"),sQuery(id+"F2.wireOp",EDGE,"E8.trimOffspring"),sQuery(id+"F2.wireOp",EDGE,"E10")])]}),"instanceName":"1"});
            deleteBodies(context, id + "F40", {"entities" : qUnion([Q0])});
        }
        {
            var Q0;
            Q0=makeQuery(id+"F17.opPattern","COPY",BODY,{"derivedFrom":makeQuery(id+"F3.opExtrude","SWEPT_BODY",BODY,{"disambiguationData":[OSD([sQuery(id+"F0.wireOp",EDGE,"E0"),sQuery(id+"F2.wireOp",EDGE,"E1"),sQuery(id+"F2.wireOp",EDGE,"E2"),sQuery(id+"F2.wireOp",EDGE,"E3"),sQuery(id+"F2.wireOp",EDGE,"E4"),sQuery(id+"F2.wireOp",EDGE,"E5.MirrorCS"),sQuery(id+"F2.wireOp",EDGE,"E6.MirrorCS"),sQuery(id+"F2.wireOp",EDGE,"E7.MirrorCS"),sQuery(id+"F2.wireOp",EDGE,"E8.trimOffspring"),sQuery(id+"F2.wireOp",EDGE,"E10")])]}),"instanceName":"1"});
            deleteBodies(context, id + "F41", {"entities" : qUnion([Q0])});
        }
        {
            var Q0;
            Q0=makeQuery(id+"F19.opPattern","COPY",BODY,{"derivedFrom":makeQuery(id+"F13.opExtrude","SWEPT_BODY",BODY,{"disambiguationData":[OSD([sQuery(id+"F12.wireOp",EDGE,"E11")])]}),"instanceName":"1"});
            deleteBodies(context, id + "F42", {"entities" : qUnion([Q0])});
        }
        {
            var Q0;
            Q0=makeQuery(id+"F24.opPattern","COPY",BODY,{"derivedFrom":makeQuery(id+"F21.opPattern","COPY",BODY,{"derivedFrom":makeQuery(id+"F20.opPattern","COPY",BODY,{"derivedFrom":makeQuery(id+"F17.opPattern","COPY",BODY,{"derivedFrom":makeQuery(id+"F3.opExtrude","SWEPT_BODY",BODY,{"disambiguationData":[OSD([sQuery(id+"F0.wireOp",EDGE,"E0"),sQuery(id+"F2.wireOp",EDGE,"E1"),sQuery(id+"F2.wireOp",EDGE,"E2"),sQuery(id+"F2.wireOp",EDGE,"E3"),sQuery(id+"F2.wireOp",EDGE,"E4"),sQuery(id+"F2.wireOp",EDGE,"E5.MirrorCS"),sQuery(id+"F2.wireOp",EDGE,"E6.MirrorCS"),sQuery(id+"F2.wireOp",EDGE,"E7.MirrorCS"),sQuery(id+"F2.wireOp",EDGE,"E8.trimOffspring"),sQuery(id+"F2.wireOp",EDGE,"E10")])]}),"instanceName":"1"}),"instanceName":"1"}),"instanceName":"1"}),"instanceName":"1"});
            deleteBodies(context, id + "F43", {"entities" : qUnion([Q0])});
        }
        {
            var Q0;
            Q0=makeQuery(id+"F26.opPattern","COPY",BODY,{"derivedFrom":makeQuery(id+"F24.opPattern","COPY",BODY,{"derivedFrom":makeQuery(id+"F21.opPattern","COPY",BODY,{"derivedFrom":makeQuery(id+"F20.opPattern","COPY",BODY,{"derivedFrom":makeQuery(id+"F17.opPattern","COPY",BODY,{"derivedFrom":makeQuery(id+"F3.opExtrude","SWEPT_BODY",BODY,{"disambiguationData":[OSD([sQuery(id+"F0.wireOp",EDGE,"E0"),sQuery(id+"F2.wireOp",EDGE,"E1"),sQuery(id+"F2.wireOp",EDGE,"E2"),sQuery(id+"F2.wireOp",EDGE,"E3"),sQuery(id+"F2.wireOp",EDGE,"E4"),sQuery(id+"F2.wireOp",EDGE,"E5.MirrorCS"),sQuery(id+"F2.wireOp",EDGE,"E6.MirrorCS"),sQuery(id+"F2.wireOp",EDGE,"E7.MirrorCS"),sQuery(id+"F2.wireOp",EDGE,"E8.trimOffspring"),sQuery(id+"F2.wireOp",EDGE,"E10")])]}),"instanceName":"1"}),"instanceName":"1"}),"instanceName":"1"}),"instanceName":"1"}),"instanceName":"1"});
            deleteBodies(context, id + "F44", {"entities" : qUnion([Q0])});
        }
        {
            var Q0;
            Q0=makeQuery(id+"F29.opPattern","COPY",BODY,{"derivedFrom":makeQuery(id+"F25.opPattern","COPY",BODY,{"derivedFrom":makeQuery(id+"F19.opPattern","COPY",BODY,{"derivedFrom":makeQuery(id+"F13.opExtrude","SWEPT_BODY",BODY,{"disambiguationData":[OSD([sQuery(id+"F12.wireOp",EDGE,"E11")])]}),"instanceName":"1"}),"instanceName":"1"}),"instanceName":"1"});
            deleteBodies(context, id + "F45", {"entities" : qUnion([Q0])});
        }
        {
            var Q0;
            Q0=makeQuery(id+"F33.opPattern","COPY",BODY,{"derivedFrom":makeQuery(id+"F31.opPattern","COPY",BODY,{"derivedFrom":makeQuery(id+"F28.opPattern","COPY",BODY,{"derivedFrom":makeQuery(id+"F26.opPattern","COPY",BODY,{"derivedFrom":makeQuery(id+"F24.opPattern","COPY",BODY,{"derivedFrom":makeQuery(id+"F21.opPattern","COPY",BODY,{"derivedFrom":makeQuery(id+"F20.opPattern","COPY",BODY,{"derivedFrom":makeQuery(id+"F17.opPattern","COPY",BODY,{"derivedFrom":makeQuery(id+"F3.opExtrude","SWEPT_BODY",BODY,{"disambiguationData":[OSD([sQuery(id+"F0.wireOp",EDGE,"E0"),sQuery(id+"F2.wireOp",EDGE,"E1"),sQuery(id+"F2.wireOp",EDGE,"E2"),sQuery(id+"F2.wireOp",EDGE,"E3"),sQuery(id+"F2.wireOp",EDGE,"E4"),sQuery(id+"F2.wireOp",EDGE,"E5.MirrorCS"),sQuery(id+"F2.wireOp",EDGE,"E6.MirrorCS"),sQuery(id+"F2.wireOp",EDGE,"E7.MirrorCS"),sQuery(id+"F2.wireOp",EDGE,"E8.trimOffspring"),sQuery(id+"F2.wireOp",EDGE,"E10")])]}),"instanceName":"1"}),"instanceName":"1"}),"instanceName":"1"}),"instanceName":"1"}),"instanceName":"1"}),"instanceName":"1"}),"instanceName":"1"}),"instanceName":"1"});
            deleteBodies(context, id + "F46", {"entities" : qUnion([Q0])});
        }
        {
            var Q0;
            Q0=makeQuery(id+"F35.opPattern","COPY",BODY,{"derivedFrom":makeQuery(id+"F33.opPattern","COPY",BODY,{"derivedFrom":makeQuery(id+"F31.opPattern","COPY",BODY,{"derivedFrom":makeQuery(id+"F28.opPattern","COPY",BODY,{"derivedFrom":makeQuery(id+"F26.opPattern","COPY",BODY,{"derivedFrom":makeQuery(id+"F24.opPattern","COPY",BODY,{"derivedFrom":makeQuery(id+"F21.opPattern","COPY",BODY,{"derivedFrom":makeQuery(id+"F20.opPattern","COPY",BODY,{"derivedFrom":makeQuery(id+"F17.opPattern","COPY",BODY,{"derivedFrom":makeQuery(id+"F3.opExtrude","SWEPT_BODY",BODY,{"disambiguationData":[OSD([sQuery(id+"F0.wireOp",EDGE,"E0"),sQuery(id+"F2.wireOp",EDGE,"E1"),sQuery(id+"F2.wireOp",EDGE,"E2"),sQuery(id+"F2.wireOp",EDGE,"E3"),sQuery(id+"F2.wireOp",EDGE,"E4"),sQuery(id+"F2.wireOp",EDGE,"E5.MirrorCS"),sQuery(id+"F2.wireOp",EDGE,"E6.MirrorCS"),sQuery(id+"F2.wireOp",EDGE,"E7.MirrorCS"),sQuery(id+"F2.wireOp",EDGE,"E8.trimOffspring"),sQuery(id+"F2.wireOp",EDGE,"E10")])]}),"instanceName":"1"}),"instanceName":"1"}),"instanceName":"1"}),"instanceName":"1"}),"instanceName":"1"}),"instanceName":"1"}),"instanceName":"1"}),"instanceName":"1"}),"instanceName":"1"});
            deleteBodies(context, id + "F47", {"entities" : qUnion([Q0])});
        }
        {
            var Q0;
            Q0=makeQuery(id+"F38.opPattern","COPY",BODY,{"derivedFrom":makeQuery(id+"F34.opPattern","COPY",BODY,{"derivedFrom":makeQuery(id+"F29.opPattern","COPY",BODY,{"derivedFrom":makeQuery(id+"F25.opPattern","COPY",BODY,{"derivedFrom":makeQuery(id+"F19.opPattern","COPY",BODY,{"derivedFrom":makeQuery(id+"F13.opExtrude","SWEPT_BODY",BODY,{"disambiguationData":[OSD([sQuery(id+"F12.wireOp",EDGE,"E11")])]}),"instanceName":"1"}),"instanceName":"1"}),"instanceName":"1"}),"instanceName":"1"}),"instanceName":"1"});
            deleteBodies(context, id + "F48", {"entities" : qUnion([Q0])});
        }
        {
            var Q0;
            Q0=makeQuery(id+"F20.opPattern","COPY",BODY,{"derivedFrom":makeQuery(id+"F17.opPattern","COPY",BODY,{"derivedFrom":makeQuery(id+"F3.opExtrude","SWEPT_BODY",BODY,{"disambiguationData":[OSD([sQuery(id+"F0.wireOp",EDGE,"E0"),sQuery(id+"F2.wireOp",EDGE,"E1"),sQuery(id+"F2.wireOp",EDGE,"E2"),sQuery(id+"F2.wireOp",EDGE,"E3"),sQuery(id+"F2.wireOp",EDGE,"E4"),sQuery(id+"F2.wireOp",EDGE,"E5.MirrorCS"),sQuery(id+"F2.wireOp",EDGE,"E6.MirrorCS"),sQuery(id+"F2.wireOp",EDGE,"E7.MirrorCS"),sQuery(id+"F2.wireOp",EDGE,"E8.trimOffspring"),sQuery(id+"F2.wireOp",EDGE,"E10")])]}),"instanceName":"1"}),"instanceName":"1"});
            deleteBodies(context, id + "F49", {"entities" : qUnion([Q0])});
        }
        {
            var Q0;
            Q0=makeQuery(id+"F3.opExtrude","SWEPT_BODY",BODY,{"disambiguationData":[OSD([sQuery(id+"F0.wireOp",EDGE,"E0"),sQuery(id+"F2.wireOp",EDGE,"E1"),sQuery(id+"F2.wireOp",EDGE,"E2"),sQuery(id+"F2.wireOp",EDGE,"E3"),sQuery(id+"F2.wireOp",EDGE,"E4"),sQuery(id+"F2.wireOp",EDGE,"E5.MirrorCS"),sQuery(id+"F2.wireOp",EDGE,"E6.MirrorCS"),sQuery(id+"F2.wireOp",EDGE,"E7.MirrorCS"),sQuery(id+"F2.wireOp",EDGE,"E8.trimOffspring"),sQuery(id+"F2.wireOp",EDGE,"E10")])]});
            transform(context, id + "F50", {"entities" : qUnion([Q0]), "transformType" : TransformType.TRANSLATION_3D, "dx" : 0 * mm, "dy" : 45 * mm, "dz" : 0 * mm, "makeCopy" : true});
        }
        {
            var Q0;
            Q0=makeQuery(id+"F28.opPattern","COPY",BODY,{"derivedFrom":makeQuery(id+"F26.opPattern","COPY",BODY,{"derivedFrom":makeQuery(id+"F24.opPattern","COPY",BODY,{"derivedFrom":makeQuery(id+"F21.opPattern","COPY",BODY,{"derivedFrom":makeQuery(id+"F20.opPattern","COPY",BODY,{"derivedFrom":makeQuery(id+"F17.opPattern","COPY",BODY,{"derivedFrom":makeQuery(id+"F3.opExtrude","SWEPT_BODY",BODY,{"disambiguationData":[OSD([sQuery(id+"F0.wireOp",EDGE,"E0"),sQuery(id+"F2.wireOp",EDGE,"E1"),sQuery(id+"F2.wireOp",EDGE,"E2"),sQuery(id+"F2.wireOp",EDGE,"E3"),sQuery(id+"F2.wireOp",EDGE,"E4"),sQuery(id+"F2.wireOp",EDGE,"E5.MirrorCS"),sQuery(id+"F2.wireOp",EDGE,"E6.MirrorCS"),sQuery(id+"F2.wireOp",EDGE,"E7.MirrorCS"),sQuery(id+"F2.wireOp",EDGE,"E8.trimOffspring"),sQuery(id+"F2.wireOp",EDGE,"E10")])]}),"instanceName":"1"}),"instanceName":"1"}),"instanceName":"1"}),"instanceName":"1"}),"instanceName":"1"}),"instanceName":"1"});
            deleteBodies(context, id + "F51", {"entities" : qUnion([Q0])});
        }
        {
            var Q0;
            Q0=makeQuery(id+"F21.opPattern","COPY",BODY,{"derivedFrom":makeQuery(id+"F20.opPattern","COPY",BODY,{"derivedFrom":makeQuery(id+"F17.opPattern","COPY",BODY,{"derivedFrom":makeQuery(id+"F3.opExtrude","SWEPT_BODY",BODY,{"disambiguationData":[OSD([sQuery(id+"F0.wireOp",EDGE,"E0"),sQuery(id+"F2.wireOp",EDGE,"E1"),sQuery(id+"F2.wireOp",EDGE,"E2"),sQuery(id+"F2.wireOp",EDGE,"E3"),sQuery(id+"F2.wireOp",EDGE,"E4"),sQuery(id+"F2.wireOp",EDGE,"E5.MirrorCS"),sQuery(id+"F2.wireOp",EDGE,"E6.MirrorCS"),sQuery(id+"F2.wireOp",EDGE,"E7.MirrorCS"),sQuery(id+"F2.wireOp",EDGE,"E8.trimOffspring"),sQuery(id+"F2.wireOp",EDGE,"E10")])]}),"instanceName":"1"}),"instanceName":"1"}),"instanceName":"1"});
            transform(context, id + "F52", {"entities" : qUnion([Q0]), "transformType" : TransformType.TRANSLATION_3D, "dx" : 0 * mm, "dy" : 45 * mm, "dz" : 0 * mm, "makeCopy" : true});
        }
        {
            var Q0;
            Q0=makeQuery(id+"F37.opPattern","COPY",BODY,{"derivedFrom":makeQuery(id+"F35.opPattern","COPY",BODY,{"derivedFrom":makeQuery(id+"F33.opPattern","COPY",BODY,{"derivedFrom":makeQuery(id+"F31.opPattern","COPY",BODY,{"derivedFrom":makeQuery(id+"F28.opPattern","COPY",BODY,{"derivedFrom":makeQuery(id+"F26.opPattern","COPY",BODY,{"derivedFrom":makeQuery(id+"F24.opPattern","COPY",BODY,{"derivedFrom":makeQuery(id+"F21.opPattern","COPY",BODY,{"derivedFrom":makeQuery(id+"F20.opPattern","COPY",BODY,{"derivedFrom":makeQuery(id+"F17.opPattern","COPY",BODY,{"derivedFrom":makeQuery(id+"F3.opExtrude","SWEPT_BODY",BODY,{"disambiguationData":[OSD([sQuery(id+"F0.wireOp",EDGE,"E0"),sQuery(id+"F2.wireOp",EDGE,"E1"),sQuery(id+"F2.wireOp",EDGE,"E2"),sQuery(id+"F2.wireOp",EDGE,"E3"),sQuery(id+"F2.wireOp",EDGE,"E4"),sQuery(id+"F2.wireOp",EDGE,"E5.MirrorCS"),sQuery(id+"F2.wireOp",EDGE,"E6.MirrorCS"),sQuery(id+"F2.wireOp",EDGE,"E7.MirrorCS"),sQuery(id+"F2.wireOp",EDGE,"E8.trimOffspring"),sQuery(id+"F2.wireOp",EDGE,"E10")])]}),"instanceName":"1"}),"instanceName":"1"}),"instanceName":"1"}),"instanceName":"1"}),"instanceName":"1"}),"instanceName":"1"}),"instanceName":"1"}),"instanceName":"1"}),"instanceName":"1"}),"instanceName":"1"});
            deleteBodies(context, id + "F53", {"entities" : qUnion([Q0])});
        }
        {
            var Q0;
            Q0=makeQuery(id+"F31.opPattern","COPY",BODY,{"derivedFrom":makeQuery(id+"F28.opPattern","COPY",BODY,{"derivedFrom":makeQuery(id+"F26.opPattern","COPY",BODY,{"derivedFrom":makeQuery(id+"F24.opPattern","COPY",BODY,{"derivedFrom":makeQuery(id+"F21.opPattern","COPY",BODY,{"derivedFrom":makeQuery(id+"F20.opPattern","COPY",BODY,{"derivedFrom":makeQuery(id+"F17.opPattern","COPY",BODY,{"derivedFrom":makeQuery(id+"F3.opExtrude","SWEPT_BODY",BODY,{"disambiguationData":[OSD([sQuery(id+"F0.wireOp",EDGE,"E0"),sQuery(id+"F2.wireOp",EDGE,"E1"),sQuery(id+"F2.wireOp",EDGE,"E2"),sQuery(id+"F2.wireOp",EDGE,"E3"),sQuery(id+"F2.wireOp",EDGE,"E4"),sQuery(id+"F2.wireOp",EDGE,"E5.MirrorCS"),sQuery(id+"F2.wireOp",EDGE,"E6.MirrorCS"),sQuery(id+"F2.wireOp",EDGE,"E7.MirrorCS"),sQuery(id+"F2.wireOp",EDGE,"E8.trimOffspring"),sQuery(id+"F2.wireOp",EDGE,"E10")])]}),"instanceName":"1"}),"instanceName":"1"}),"instanceName":"1"}),"instanceName":"1"}),"instanceName":"1"}),"instanceName":"1"}),"instanceName":"1"});
            transform(context, id + "F54", {"entities" : qUnion([Q0]), "transformType" : TransformType.TRANSLATION_3D, "dx" : 0 * mm, "dy" : 45 * mm, "dz" : 0 * mm, "makeCopy" : true});
        }
        {
            var Q0;
            Q0=makeQuery(id+"F1.opExtrude","CAP_FACE",FACE,{"disambiguationData":[OSD([sQuery(id+"F0.wireOp",EDGE,"E0")])],"isStart":false});
            var sketch = newSketch(context, id + "F55", { "sketchPlane" : qUnion([Q0])});
            skSolve(sketch);
        }
        {
            var Q0;
            Q0=makeQuery(id+"F55.imprint","IMPRINT",FACE,{"disambiguationData":[TD([[makeQuery(id+"F55.imprint","IMPRINT",EDGE,{"derivedFrom":makeQuery(id+"F1.opExtrude","CAP_EDGE",EDGE,{"disambiguationData":[OSD([sQuery(id+"F0.wireOp",EDGE,"E0")])],"isStart":false})}),1.0]])]});
            extrude(context, id + "F56", {"entities" : qUnion([Q0]), "operationType" : NewBodyOperationType.REMOVE, "oppositeDirection" : true, "depth" : 80 * mm, "offsetDistance" : 25 * mm});
        }
    });
